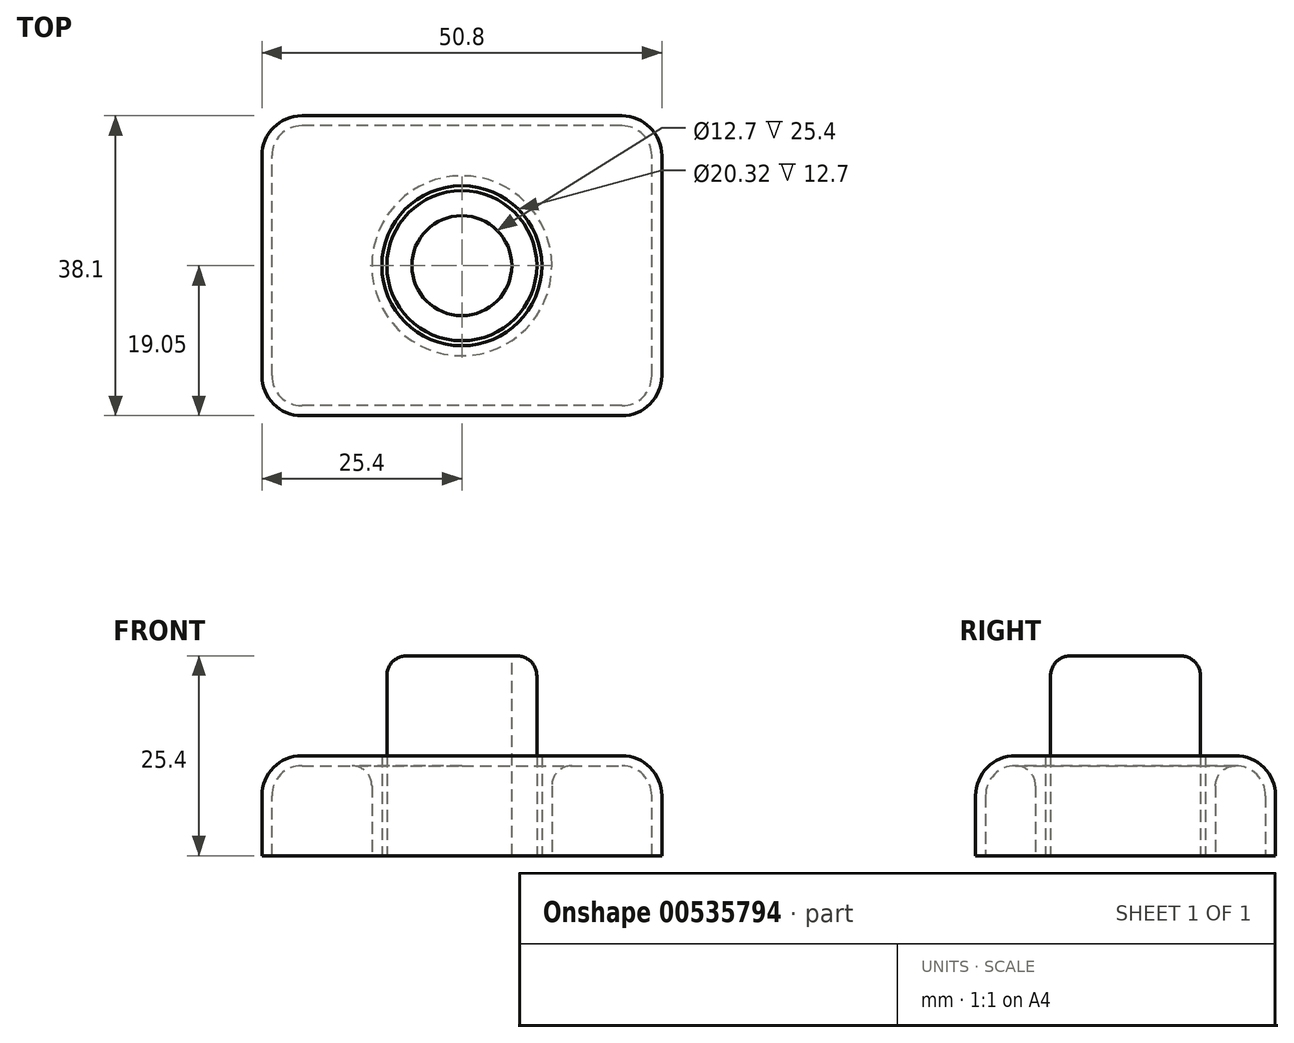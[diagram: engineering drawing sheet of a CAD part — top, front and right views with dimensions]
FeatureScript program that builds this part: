
annotation { "Feature Type Name" : "Feature", "Feature Type Description" : "" }
export const myFeature = defineFeature(function(context is Context, id is Id, definition is map)
    precondition{}
    {
        {
            var Q0;
            Q0=qCreatedBy(makeId("Top.planeOp"),FACE);
            var sketch = newSketch(context, id + "F0", { "sketchPlane" : qUnion([Q0])});
            skCircle(sketch, "E0", {"center": v(0, 0) * mm, "radius": 9.53 * mm});
            skCircle(sketch, "E1", {"center": v(0, 0) * mm, "radius": 10.16 * mm});
            skLineSegment(sketch, "E2.bottom", {"start": v(25.4, -19.05) * mm, "end": v(-25.4, -19.05) * mm});
            skLineSegment(sketch, "E2.top", {"start": v(25.4, 19.05) * mm, "end": v(-25.4, 19.05) * mm});
            skLineSegment(sketch, "E2.left", {"start": v(25.4, -19.05) * mm, "end": v(25.4, 19.05) * mm});
            skLineSegment(sketch, "E2.right", {"start": v(-25.4, -19.05) * mm, "end": v(-25.4, 19.05) * mm});
            skSolve(sketch);
        }
        {
            var Q0;
            Q0=makeQuery(id+"F0.imprint","IMPRINT",FACE,{"disambiguationData":[TD([[makeQuery(id+"F0.imprint","IMPRINT",EDGE,{"derivedFrom":sQuery(id+"F0.wireOp",EDGE,"E1")}),-1.0]])]});
            extrude(context, id + "F1", {"entities" : qUnion([Q0]), "depth" : 12.7 * mm, "offsetDistance" : 25.4 * mm});
        }
        {
            var Q0;
            Q0=makeQuery(id+"F0.imprint","IMPRINT",FACE,{"disambiguationData":[TD([[makeQuery(id+"F0.imprint","IMPRINT",EDGE,{"derivedFrom":sQuery(id+"F0.wireOp",EDGE,"E0")}),1.0]])]});
            extrude(context, id + "F2", {"entities" : qUnion([Q0]), "depth" : 25.4 * mm, "offsetDistance" : 25.4 * mm});
        }
        {
            var Q0;
            Q0=makeQuery(id+"F1.opExtrude","SWEPT_EDGE",EDGE,{"disambiguationData":[OSD([sQuery(id+"F0.wireOp",EDGE,"E2.bottom"),sQuery(id+"F0.wireOp",EDGE,"E2.left")])]});
            var Q1;
            Q1=makeQuery(id+"F1.opExtrude","SWEPT_EDGE",EDGE,{"disambiguationData":[OSD([sQuery(id+"F0.wireOp",EDGE,"E2.top"),sQuery(id+"F0.wireOp",EDGE,"E2.left")])]});
            var Q2;
            Q2=makeQuery(id+"F1.opExtrude","SWEPT_EDGE",EDGE,{"disambiguationData":[OSD([sQuery(id+"F0.wireOp",EDGE,"E2.bottom"),sQuery(id+"F0.wireOp",EDGE,"E2.right")])]});
            var Q3;
            Q3=makeQuery(id+"F1.opExtrude","SWEPT_EDGE",EDGE,{"disambiguationData":[OSD([sQuery(id+"F0.wireOp",EDGE,"E2.top"),sQuery(id+"F0.wireOp",EDGE,"E2.right")])]});
            fillet(context, id + "F3", {"entities" : qUnion([Q0, Q1, Q2, Q3]), "radius" : 5.08 * mm, "tangentPropagation" : true, "allowEdgeOverflow" : false});
        }
        {
            var Q0;
            Q0=makeQuery(id+"F2.opExtrude","CAP_EDGE",EDGE,{"disambiguationData":[OSD([sQuery(id+"F0.wireOp",EDGE,"E0")])],"isStart":false});
            fillet(context, id + "F4", {"entities" : qUnion([Q0]), "radius" : 2.54 * mm, "tangentPropagation" : true, "allowEdgeOverflow" : false});
        }
        {
            var Q0;
            Q0=makeQuery(id+"F1.opExtrude","CAP_EDGE",EDGE,{"disambiguationData":[OSD([sQuery(id+"F0.wireOp",EDGE,"E2.left")])],"isStart":false});
            fillet(context, id + "F5", {"entities" : qUnion([Q0]), "radius" : 5.08 * mm, "tangentPropagation" : true, "allowEdgeOverflow" : false});
        }
        {
            var Q0;
            Q0=makeQuery(id+"F1.opExtrude","CAP_FACE",FACE,{"disambiguationData":[OSD([sQuery(id+"F0.wireOp",EDGE,"E1"),sQuery(id+"F0.wireOp",EDGE,"E2.bottom"),sQuery(id+"F0.wireOp",EDGE,"E2.top"),sQuery(id+"F0.wireOp",EDGE,"E2.left"),sQuery(id+"F0.wireOp",EDGE,"E2.right")])],"isStart":true});
            shell(context, id + "F6", {"entities" : qUnion([Q0]), "thickness" : 1.27 * mm});
        }
        {
            var Q0;
            {var subQ0=sQuery(id+"F0.wireOp",EDGE,"E1");Q0=makeQuery(id+"F6.opShell","OFFSET_EDGE",EDGE,{"disambiguationData":[OSD([subQ0]),TDD([makeQuery(id+"F1.opExtrude","CAP_EDGE",EDGE,{"disambiguationData":[OSD([subQ0])],"isStart":false})])]});}
            fillet(context, id + "F7", {"entities" : qUnion([Q0]), "radius" : 2.54 * mm, "tangentPropagation" : true, "allowEdgeOverflow" : false});
        }
        {
            var Q0;
            Q0=makeQuery(id+"F2.opExtrude","CAP_FACE",FACE,{"disambiguationData":[OSD([sQuery(id+"F0.wireOp",EDGE,"E0")])],"isStart":false});
            var sketch = newSketch(context, id + "F8", { "sketchPlane" : qUnion([Q0])});
            skCircle(sketch, "E3", {"center": v(0, 0) * mm, "radius": 6.35 * mm});
            skSolve(sketch);
        }
        {
            var Q0;
            Q0 = qSketchRegion(id + "F8", true);
            extrude(context, id + "F9", {"entities" : qUnion([Q0]), "operationType" : NewBodyOperationType.REMOVE, "endBound" : BoundingType.THROUGH_ALL, "oppositeDirection" : true, "depth" : 25.4 * mm, "offsetDistance" : 25.4 * mm});
        }
    });
